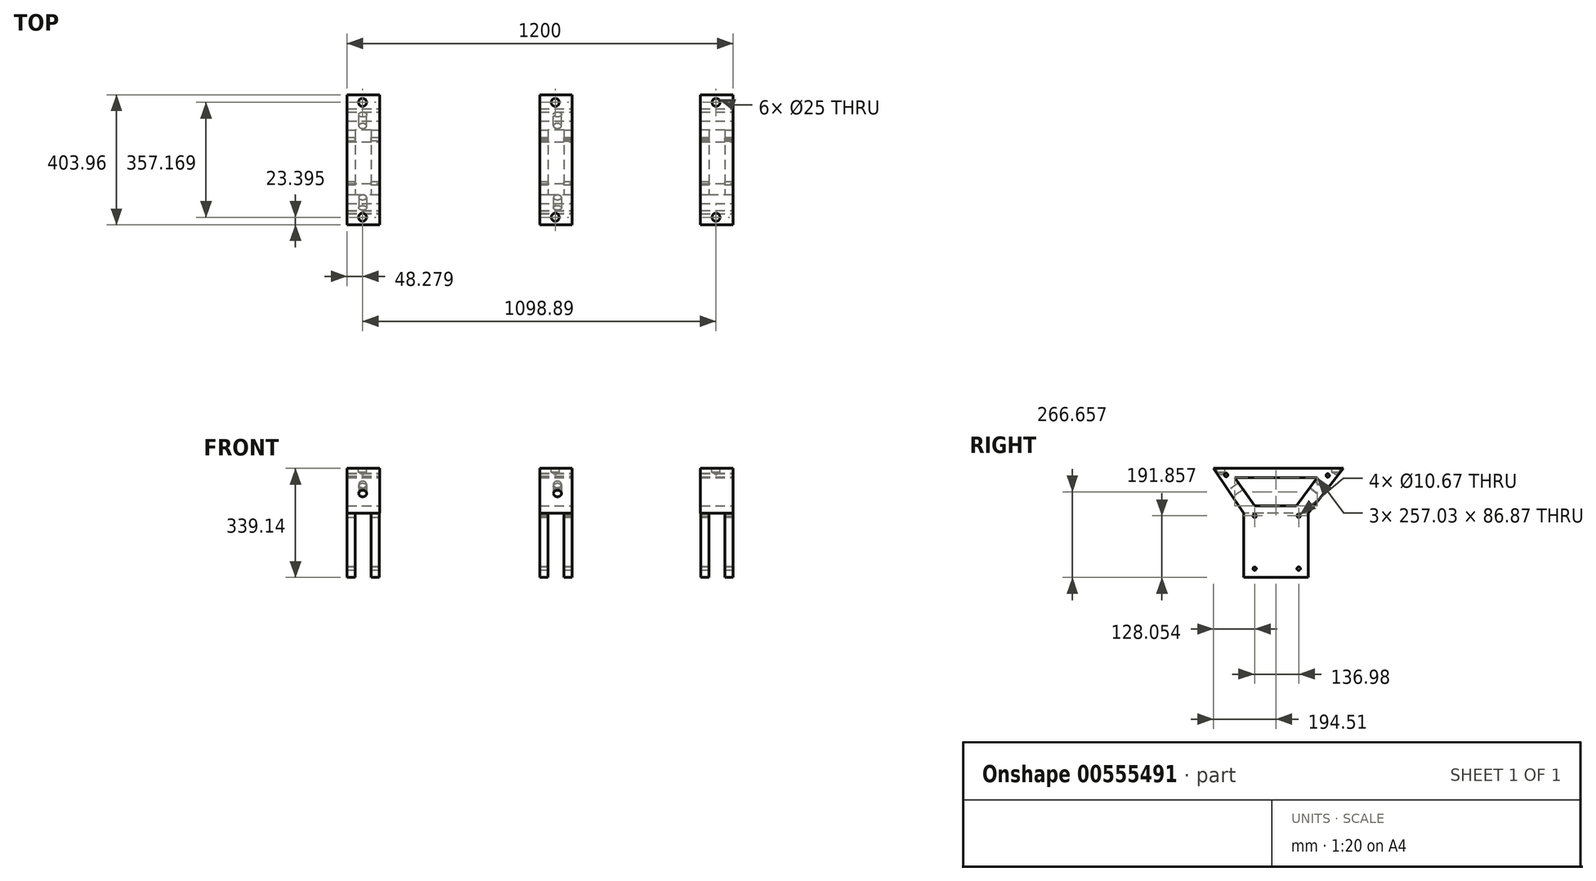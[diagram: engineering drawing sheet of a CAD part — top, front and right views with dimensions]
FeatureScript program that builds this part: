
annotation { "Feature Type Name" : "Feature", "Feature Type Description" : "" }
export const myFeature = defineFeature(function(context is Context, id is Id, definition is map)
    precondition{}
    {
        {
            var Q0;
            Q0=qCreatedBy(makeId("Front.planeOp"),FACE);
            var sketch = newSketch(context, id + "F0", { "sketchPlane" : qUnion([Q0])});
            skLineSegment(sketch, "E0.bottom", {"start": v(-163.42, 57.04) * mm, "end": v(-63.42, 57.04) * mm});
            skLineSegment(sketch, "E0.top", {"start": v(-163.42, -142.96) * mm, "end": v(-63.42, -142.96) * mm});
            skLineSegment(sketch, "E0.left", {"start": v(-163.42, 57.04) * mm, "end": v(-163.42, -142.96) * mm});
            skLineSegment(sketch, "E0.right", {"start": v(-63.42, 57.04) * mm, "end": v(-63.42, -142.96) * mm});
            skLineSegment(sketch, "E1.bottom", {"start": v(936.58, 57.04) * mm, "end": v(1036.58, 57.04) * mm});
            skLineSegment(sketch, "E1.top", {"start": v(936.58, -142.96) * mm, "end": v(1036.58, -142.96) * mm});
            skLineSegment(sketch, "E1.left", {"start": v(936.58, 57.04) * mm, "end": v(936.58, -142.96) * mm});
            skLineSegment(sketch, "E1.right", {"start": v(1036.58, 57.04) * mm, "end": v(1036.58, -142.96) * mm});
            skLineSegment(sketch, "E2.bottom", {"start": v(436.58, 57.04) * mm, "end": v(536.58, 57.04) * mm});
            skLineSegment(sketch, "E2.top", {"start": v(436.58, -142.96) * mm, "end": v(536.58, -142.96) * mm});
            skLineSegment(sketch, "E2.left", {"start": v(436.58, 57.04) * mm, "end": v(436.58, -142.96) * mm});
            skLineSegment(sketch, "E2.right", {"start": v(536.58, 57.04) * mm, "end": v(536.58, -142.96) * mm});
            skSolve(sketch);
        }
        {
            var Q0;
            Q0 = qSketchRegion(id + "F0", true);
            extrude(context, id + "F1", {"entities" : qUnion([Q0]), "depth" : 200 * mm, "offsetDistance" : 25 * mm});
        }
        {
            var Q0;
            Q0=makeQuery(id+"F1.opExtrude","SWEPT_FACE",FACE,{"disambiguationData":[OSD([sQuery(id+"F0.wireOp",EDGE,"E1.right")])]});
            var sketch = newSketch(context, id + "F2", { "sketchPlane" : qUnion([Q0])});
            skSolve(sketch);
        }
        {
            var Q0;
            {var subQ0=sQuery(id+"F0.wireOp",EDGE,"E1.right");Q0=makeQuery(id+"F2.imprint","IMPRINT",FACE,{"disambiguationData":[TD([[makeQuery(id+"F2.imprint","IMPRINT",EDGE,{"derivedFrom":makeQuery(id+"F1.opExtrude","CAP_EDGE",EDGE,{"disambiguationData":[OSD([subQ0])],"isStart":true})}),-1.0]])]});}
            var sketch = newSketch(context, id + "F3", { "sketchPlane" : qUnion([Q0])});
            skLineSegment(sketch, "E3", {"start": v(-199.96, 56.98) * mm, "end": v(-294.17, 196.18) * mm});
            skLineSegment(sketch, "E4", {"start": v(0, 56.94) * mm, "end": v(109.79, 196.18) * mm});
            skLineSegment(sketch, "E5", {"start": v(109.79, 196.18) * mm, "end": v(-294.17, 196.18) * mm});
            skLineSegment(sketch, "E6", {"start": v(-199.96, 56.98) * mm, "end": v(-96.96, 56.9) * mm});
            skLineSegment(sketch, "E7", {"start": v(-96.96, 56.9) * mm, "end": v(0, 56.94) * mm});
            skSolve(sketch);
        }
        {
            var Q0;
            Q0 = qSketchRegion(id + "F3", true);
            extrude(context, id + "F4", {"entities" : qUnion([Q0]), "oppositeDirection" : true, "depth" : 1200 * mm, "offsetDistance" : 25 * mm});
        }
        {
            var Q0;
            Q0=makeQuery(id+"F4.opExtrude","CAP_FACE",FACE,{"disambiguationData":[OSD([sQuery(id+"F3.wireOp",EDGE,"E3"),sQuery(id+"F3.wireOp",EDGE,"E4"),sQuery(id+"F3.wireOp",EDGE,"E5"),sQuery(id+"F3.wireOp",EDGE,"E6"),sQuery(id+"F3.wireOp",EDGE,"E7")])],"isStart":true});
            var sketch = newSketch(context, id + "F5", { "sketchPlane" : qUnion([Q0])});
            skLineSegment(sketch, "E8", {"start": v(-228.17, 167.13) * mm, "end": v(28.85, 167.13) * mm});
            skLineSegment(sketch, "E9", {"start": v(28.85, 167.13) * mm, "end": v(-36.76, 80.26) * mm});
            skLineSegment(sketch, "E10", {"start": v(-36.76, 80.26) * mm, "end": v(-166.23, 80.26) * mm});
            skLineSegment(sketch, "E11", {"start": v(-166.23, 80.26) * mm, "end": v(-228.17, 167.13) * mm});
            skSolve(sketch);
        }
        {
            var Q0;
            Q0 = qSketchRegion(id + "F5", true);
            extrude(context, id + "F6", {"entities" : qUnion([Q0]), "operationType" : NewBodyOperationType.REMOVE, "endBound" : BoundingType.THROUGH_ALL, "oppositeDirection" : true, "depth" : 25 * mm, "offsetDistance" : 25 * mm});
        }
        {
            var Q0;
            Q0=makeQuery(id+"F4.opExtrude","SWEPT_FACE",FACE,{"disambiguationData":[OSD([sQuery(id+"F3.wireOp",EDGE,"E3")])]});
            var sketch = newSketch(context, id + "F7", { "sketchPlane" : qUnion([Q0])});
            skLineSegment(sketch, "E12", {"start": v(-62.3, -22.73) * mm, "end": v(-62.3, 343.78) * mm});
            skLineSegment(sketch, "E13", {"start": v(435.52, -29.2) * mm, "end": v(435.52, 412.26) * mm});
            skLineSegment(sketch, "E14", {"start": v(435.52, 412.26) * mm, "end": v(-62.3, 343.78) * mm});
            skLineSegment(sketch, "E15", {"start": v(-62.3, -22.73) * mm, "end": v(435.52, -29.2) * mm});
            skSolve(sketch);
        }
        {
            var Q0;
            Q0 = qSketchRegion(id + "F7", true);
            extrude(context, id + "F8", {"entities" : qUnion([Q0]), "operationType" : NewBodyOperationType.REMOVE, "endBound" : BoundingType.THROUGH_ALL, "oppositeDirection" : true, "depth" : 25 * mm, "offsetDistance" : 25 * mm});
        }
        {
            var Q0;
            {var subQ2=sQuery(id+"F3.wireOp",EDGE,"E3");Q0=makeQuery(id+"F8.boolean.opBoolean","SPLIT",FACE,{"disambiguationData":[TD([makeQuery(id+"F8.opExtrude","SWEPT_FACE",FACE,{"disambiguationData":[OSD([sQuery(id+"F7.wireOp",EDGE,"E13")])]})])],"derivedFrom":makeQuery(id+"F4.opExtrude","SWEPT_FACE",FACE,{"disambiguationData":[OSD([subQ2])]})});}
            var sketch = newSketch(context, id + "F9", { "sketchPlane" : qUnion([Q0])});
            skLineSegment(sketch, "E16", {"start": v(536.96, 159.26) * mm, "end": v(536.96, 342.97) * mm});
            skLineSegment(sketch, "E17", {"start": v(935.8, 159.26) * mm, "end": v(935.8, 344.13) * mm});
            skLineSegment(sketch, "E18", {"start": v(935.8, 344.13) * mm, "end": v(536.96, 342.97) * mm});
            skLineSegment(sketch, "E19", {"start": v(536.96, 159.26) * mm, "end": v(536.96, -439.08) * mm});
            skLineSegment(sketch, "E20", {"start": v(536.96, -439.08) * mm, "end": v(935.8, -439.08) * mm});
            skLineSegment(sketch, "E21", {"start": v(935.8, -439.08) * mm, "end": v(935.8, 159.26) * mm});
            skSolve(sketch);
        }
        {
            var Q0;
            Q0 = qSketchRegion(id + "F9", true);
            extrude(context, id + "F10", {"entities" : qUnion([Q0]), "operationType" : NewBodyOperationType.REMOVE, "oppositeDirection" : true, "depth" : 425 * mm, "offsetDistance" : 25 * mm});
        }
        {
            var Q0;
            {var subQ1=sQuery(id+"F3.wireOp",EDGE,"E5");Q0=makeQuery(id+"F8.boolean.opBoolean","SPLIT",FACE,{"disambiguationData":[TD([makeQuery(id+"F8.opExtrude","SWEPT_FACE",FACE,{"disambiguationData":[OSD([sQuery(id+"F7.wireOp",EDGE,"E12")])]})])],"derivedFrom":makeQuery(id+"F4.opExtrude","SWEPT_FACE",FACE,{"disambiguationData":[OSD([subQ1])]})});}
            var sketch = newSketch(context, id + "F11", { "sketchPlane" : qUnion([Q0])});
            skCircle(sketch, "E22", {"center": v(-115.14, 86.4) * mm, "radius": 12.4 * mm});
            skCircle(sketch, "E23", {"center": v(-115.14, -270.77) * mm, "radius": 12.4 * mm});
            skCircle(sketch, "E24.1.0.0", {"center": v(484.12, 86.4) * mm, "radius": 12.4 * mm});
            skCircle(sketch, "E24.1.0.1", {"center": v(484.12, -270.77) * mm, "radius": 12.4 * mm});
            skCircle(sketch, "E24.2.0.0", {"center": v(983.75, 86.4) * mm, "radius": 12.4 * mm});
            skCircle(sketch, "E24.2.0.1", {"center": v(983.75, -270.77) * mm, "radius": 12.4 * mm});
            skSolve(sketch);
        }
        {
            var Q0;
            Q0=sQuery(id+"F11.wireOp",VERTEX,"E22.center");
            var Q1;
            Q1=sQuery(id+"F11.wireOp",VERTEX,"E23.center");
            var Q2;
            Q2=sQuery(id+"F11.wireOp",VERTEX,"E24.1.0.1.center");
            var Q3;
            Q3=sQuery(id+"F11.wireOp",VERTEX,"E24.1.0.0.center");
            var Q4;
            Q4=sQuery(id+"F11.wireOp",VERTEX,"E24.2.0.0.center");
            var Q5;
            Q5=sQuery(id+"F11.wireOp",VERTEX,"E24.2.0.1.center");
            var Q6;
            Q6=makeQuery(id+"F8.boolean.opBoolean","SPLIT",BODY,{"disambiguationData":[OD(1.0)],"derivedFrom":makeQuery(id+"F4.opExtrude","SWEPT_BODY",BODY,{"disambiguationData":[OSD([sQuery(id+"F3.wireOp",EDGE,"E3"),sQuery(id+"F3.wireOp",EDGE,"E4"),sQuery(id+"F3.wireOp",EDGE,"E5"),sQuery(id+"F3.wireOp",EDGE,"E6"),sQuery(id+"F3.wireOp",EDGE,"E7")])]})});
            var Q7;
            Q7=makeQuery(id+"F10.boolean.opBoolean","SPLIT",BODY,{"disambiguationData":[OD(1.0)],"derivedFrom":makeQuery(id+"F8.boolean.opBoolean","SPLIT",BODY,{"disambiguationData":[OD(0.0)],"derivedFrom":makeQuery(id+"F4.opExtrude","SWEPT_BODY",BODY,{"disambiguationData":[OSD([sQuery(id+"F3.wireOp",EDGE,"E3"),sQuery(id+"F3.wireOp",EDGE,"E4"),sQuery(id+"F3.wireOp",EDGE,"E5"),sQuery(id+"F3.wireOp",EDGE,"E6"),sQuery(id+"F3.wireOp",EDGE,"E7")])]})})});
            var Q8;
            Q8=makeQuery(id+"F10.boolean.opBoolean","SPLIT",BODY,{"disambiguationData":[OD(0.0)],"derivedFrom":makeQuery(id+"F8.boolean.opBoolean","SPLIT",BODY,{"disambiguationData":[OD(0.0)],"derivedFrom":makeQuery(id+"F4.opExtrude","SWEPT_BODY",BODY,{"disambiguationData":[OSD([sQuery(id+"F3.wireOp",EDGE,"E3"),sQuery(id+"F3.wireOp",EDGE,"E4"),sQuery(id+"F3.wireOp",EDGE,"E5"),sQuery(id+"F3.wireOp",EDGE,"E6"),sQuery(id+"F3.wireOp",EDGE,"E7")])]})})});
            hole(context, id + "F12", {"style" : HoleStyle.SIMPLE, "endStyle" : HoleEndStyle.BLIND, "holeDiameter" : 25 * mm, "holeDepth" : 12 * mm, "isTappedThrough" : true, "tappedDepth" : 12 * mm, "tapClearance" : 3, "locations" : qUnion([Q0, Q1, Q2, Q3, Q4, Q5]), "scope" : qUnion([Q6, Q7, Q8])});
        }
        {
            var Q0;
            Q0=makeQuery(id+"F10.boolean.opBoolean","SPLIT",BODY,{"disambiguationData":[OD(1.0)],"derivedFrom":makeQuery(id+"F8.boolean.opBoolean","SPLIT",BODY,{"disambiguationData":[OD(0.0)],"derivedFrom":makeQuery(id+"F4.opExtrude","SWEPT_BODY",BODY,{"disambiguationData":[OSD([sQuery(id+"F3.wireOp",EDGE,"E3"),sQuery(id+"F3.wireOp",EDGE,"E4"),sQuery(id+"F3.wireOp",EDGE,"E5"),sQuery(id+"F3.wireOp",EDGE,"E6"),sQuery(id+"F3.wireOp",EDGE,"E7")])]})})});
            var Q1;
            Q1=makeQuery(id+"F1.opExtrude","SWEPT_BODY",BODY,{"disambiguationData":[OSD([sQuery(id+"F0.wireOp",EDGE,"E2.bottom"),sQuery(id+"F0.wireOp",EDGE,"E2.top"),sQuery(id+"F0.wireOp",EDGE,"E2.left"),sQuery(id+"F0.wireOp",EDGE,"E2.right")])]});
            var Q2;
            Q2=makeQuery(id+"F10.boolean.opBoolean","SPLIT",BODY,{"disambiguationData":[OD(0.0)],"derivedFrom":makeQuery(id+"F8.boolean.opBoolean","SPLIT",BODY,{"disambiguationData":[OD(0.0)],"derivedFrom":makeQuery(id+"F4.opExtrude","SWEPT_BODY",BODY,{"disambiguationData":[OSD([sQuery(id+"F3.wireOp",EDGE,"E3"),sQuery(id+"F3.wireOp",EDGE,"E4"),sQuery(id+"F3.wireOp",EDGE,"E5"),sQuery(id+"F3.wireOp",EDGE,"E6"),sQuery(id+"F3.wireOp",EDGE,"E7")])]})})});
            var Q3;
            Q3=makeQuery(id+"F1.opExtrude","SWEPT_BODY",BODY,{"disambiguationData":[OSD([sQuery(id+"F0.wireOp",EDGE,"E1.bottom"),sQuery(id+"F0.wireOp",EDGE,"E1.top"),sQuery(id+"F0.wireOp",EDGE,"E1.left"),sQuery(id+"F0.wireOp",EDGE,"E1.right")])]});
            var Q4;
            Q4=makeQuery(id+"F8.boolean.opBoolean","SPLIT",BODY,{"disambiguationData":[OD(1.0)],"derivedFrom":makeQuery(id+"F4.opExtrude","SWEPT_BODY",BODY,{"disambiguationData":[OSD([sQuery(id+"F3.wireOp",EDGE,"E3"),sQuery(id+"F3.wireOp",EDGE,"E4"),sQuery(id+"F3.wireOp",EDGE,"E5"),sQuery(id+"F3.wireOp",EDGE,"E6"),sQuery(id+"F3.wireOp",EDGE,"E7")])]})});
            var Q5;
            Q5=makeQuery(id+"F1.opExtrude","SWEPT_BODY",BODY,{"disambiguationData":[OSD([sQuery(id+"F0.wireOp",EDGE,"E0.bottom"),sQuery(id+"F0.wireOp",EDGE,"E0.top"),sQuery(id+"F0.wireOp",EDGE,"E0.left"),sQuery(id+"F0.wireOp",EDGE,"E0.right")])]});
            booleanBodies(context, id + "F13", {"operationType" : BooleanOperationType.UNION, "tools" : qUnion([Q0, Q1, Q2, Q3, Q4, Q5])});
        }
        {
            var Q0;
            Q0=makeQuery(id+"F13.opBoolean","MERGE",FACE,{"derivedFrom":[makeQuery(id+"F1.opExtrude","SWEPT_FACE",FACE,{"disambiguationData":[OSD([sQuery(id+"F0.wireOp",EDGE,"E0.left")])]}),makeQuery(id+"F4.opExtrude","CAP_FACE",FACE,{"disambiguationData":[OSD([sQuery(id+"F3.wireOp",EDGE,"E3"),sQuery(id+"F3.wireOp",EDGE,"E4"),sQuery(id+"F3.wireOp",EDGE,"E5"),sQuery(id+"F3.wireOp",EDGE,"E6"),sQuery(id+"F3.wireOp",EDGE,"E7")])],"isStart":false})]});
            var sketch = newSketch(context, id + "F14", { "sketchPlane" : qUnion([Q0])});
            skCircle(sketch, "E25", {"center": v(29.14, 48.9) * mm, "radius": 5.34 * mm});
            skCircle(sketch, "E26", {"center": v(166.12, 48.9) * mm, "radius": 5.34 * mm});
            skCircle(sketch, "E27", {"center": v(29.14, -115.26) * mm, "radius": 5.35 * mm});
            skCircle(sketch, "E28", {"center": v(166.12, -115.26) * mm, "radius": 5.05 * mm});
            skSolve(sketch);
        }
        {
            var Q0;
            Q0=makeQuery(id+"F14.imprint","IMPRINT",FACE,{"disambiguationData":[TD([[makeQuery(id+"F14.imprint","IMPRINT",EDGE,{"derivedFrom":sQuery(id+"F14.wireOp",EDGE,"E26")}),1.0]])]});
            var Q1;
            Q1=makeQuery(id+"F14.imprint","IMPRINT",FACE,{"disambiguationData":[TD([[makeQuery(id+"F14.imprint","IMPRINT",EDGE,{"derivedFrom":sQuery(id+"F14.wireOp",EDGE,"E27")}),1.0]])]});
            var Q2;
            Q2=makeQuery(id+"F14.imprint","IMPRINT",FACE,{"disambiguationData":[TD([[makeQuery(id+"F14.imprint","IMPRINT",EDGE,{"derivedFrom":sQuery(id+"F14.wireOp",EDGE,"E28")}),1.0]])]});
            var Q3;
            Q3=makeQuery(id+"F14.imprint","IMPRINT",FACE,{"disambiguationData":[TD([[makeQuery(id+"F14.imprint","IMPRINT",EDGE,{"derivedFrom":sQuery(id+"F14.wireOp",EDGE,"E25")}),1.0]])]});
            extrude(context, id + "F15", {"entities" : qUnion([Q0, Q1, Q2, Q3]), "operationType" : NewBodyOperationType.REMOVE, "endBound" : BoundingType.THROUGH_ALL, "oppositeDirection" : true, "depth" : 25 * mm, "offsetDistance" : 25 * mm});
        }
        {
            var Q0;
            Q0=makeQuery(id+"F1.opExtrude","SWEPT_FACE",FACE,{"disambiguationData":[OSD([sQuery(id+"F0.wireOp",EDGE,"E2.left")])]});
            var sketch = newSketch(context, id + "F16", { "sketchPlane" : qUnion([Q0])});
            skCircle(sketch, "E29", {"center": v(29.07, 48.87) * mm, "radius": 5.34 * mm});
            skCircle(sketch, "E30", {"center": v(166.1, 48.83) * mm, "radius": 5.34 * mm});
            skCircle(sketch, "E31", {"center": v(166.1, -115.28) * mm, "radius": 5.05 * mm});
            skCircle(sketch, "E32", {"center": v(29.2, -115.26) * mm, "radius": 5.34 * mm});
            skSolve(sketch);
        }
        {
            var Q0;
            Q0 = qSketchRegion(id + "F16", true);
            extrude(context, id + "F17", {"entities" : qUnion([Q0]), "operationType" : NewBodyOperationType.REMOVE, "endBound" : BoundingType.THROUGH_ALL, "oppositeDirection" : true, "depth" : 25 * mm, "offsetDistance" : 25 * mm});
        }
        {
            var Q0;
            Q0=makeQuery(id+"F1.opExtrude","SWEPT_FACE",FACE,{"disambiguationData":[OSD([sQuery(id+"F0.wireOp",EDGE,"E1.left")])]});
            var sketch = newSketch(context, id + "F18", { "sketchPlane" : qUnion([Q0])});
            skCircle(sketch, "E33", {"center": v(166.08, 48.88) * mm, "radius": 5.34 * mm});
            skCircle(sketch, "E34", {"center": v(29.16, 48.9) * mm, "radius": 5.34 * mm});
            skCircle(sketch, "E35", {"center": v(29.12, -115.26) * mm, "radius": 5.34 * mm});
            skCircle(sketch, "E36", {"center": v(166.08, -115.29) * mm, "radius": 5.02 * mm});
            skSolve(sketch);
        }
        {
            var Q0;
            Q0 = qSketchRegion(id + "F18", true);
            extrude(context, id + "F19", {"entities" : qUnion([Q0]), "operationType" : NewBodyOperationType.REMOVE, "endBound" : BoundingType.THROUGH_ALL, "oppositeDirection" : true, "depth" : 1250 * mm, "offsetDistance" : 25 * mm});
        }
        {
            var Q0;
            {var subQ2=sQuery(id+"F3.wireOp",EDGE,"E3");Q0=makeQuery(id+"F8.boolean.opBoolean","SPLIT",FACE,{"disambiguationData":[TD([makeQuery(id+"F8.opExtrude","SWEPT_FACE",FACE,{"disambiguationData":[OSD([sQuery(id+"F7.wireOp",EDGE,"E12")])]})])],"derivedFrom":makeQuery(id+"F4.opExtrude","SWEPT_FACE",FACE,{"disambiguationData":[OSD([subQ2])]})});}
            var sketch = newSketch(context, id + "F20", { "sketchPlane" : qUnion([Q0])});
            skCircle(sketch, "E37", {"center": v(-114.59, 233.48) * mm, "radius": 10.87 * mm});
            skCircle(sketch, "E38", {"center": v(490.96, 233.48) * mm, "radius": 10.87 * mm});
            skSolve(sketch);
        }
        {
            var Q0;
            Q0=sQuery(id+"F20.wireOp",VERTEX,"E37.center");
            var Q1;
            Q1=sQuery(id+"F20.wireOp",VERTEX,"E38.center");
            var Q2;
            Q2=makeQuery(id+"F8.boolean.opBoolean","SPLIT",BODY,{"disambiguationData":[OD(1.0)],"derivedFrom":makeQuery(id+"F4.opExtrude","SWEPT_BODY",BODY,{"disambiguationData":[OSD([sQuery(id+"F3.wireOp",EDGE,"E3"),sQuery(id+"F3.wireOp",EDGE,"E4"),sQuery(id+"F3.wireOp",EDGE,"E5"),sQuery(id+"F3.wireOp",EDGE,"E6"),sQuery(id+"F3.wireOp",EDGE,"E7")])]})});
            var Q3;
            Q3=makeQuery(id+"F10.boolean.opBoolean","SPLIT",BODY,{"disambiguationData":[OD(1.0)],"derivedFrom":makeQuery(id+"F8.boolean.opBoolean","SPLIT",BODY,{"disambiguationData":[OD(0.0)],"derivedFrom":makeQuery(id+"F4.opExtrude","SWEPT_BODY",BODY,{"disambiguationData":[OSD([sQuery(id+"F3.wireOp",EDGE,"E3"),sQuery(id+"F3.wireOp",EDGE,"E4"),sQuery(id+"F3.wireOp",EDGE,"E5"),sQuery(id+"F3.wireOp",EDGE,"E6"),sQuery(id+"F3.wireOp",EDGE,"E7")])]})})});
            hole(context, id + "F21", {"style" : HoleStyle.SIMPLE, "endStyle" : HoleEndStyle.BLIND, "holeDiameter" : 25 * mm, "majorDiameter" : 5 * mm, "holeDepth" : 50 * mm, "isTappedThrough" : true, "tappedDepth" : 12 * mm, "tapClearance" : 3, "locations" : qUnion([Q0, Q1]), "scope" : qUnion([Q2, Q3])});
        }
        {
            var Q0;
            {var subQ2=sQuery(id+"F3.wireOp",EDGE,"E4");Q0=makeQuery(id+"F8.boolean.opBoolean","SPLIT",FACE,{"disambiguationData":[TD([makeQuery(id+"F8.opExtrude","SWEPT_FACE",FACE,{"disambiguationData":[OSD([sQuery(id+"F7.wireOp",EDGE,"E12")])]})])],"derivedFrom":makeQuery(id+"F4.opExtrude","SWEPT_FACE",FACE,{"disambiguationData":[OSD([subQ2])]})});}
            var sketch = newSketch(context, id + "F22", { "sketchPlane" : qUnion([Q0])});
            skCircle(sketch, "E39", {"center": v(114.65, 122.94) * mm, "radius": 11.4 * mm});
            skCircle(sketch, "E40", {"center": v(-490.77, 123.31) * mm, "radius": 10.98 * mm});
            skSolve(sketch);
        }
        {
            var Q0;
            Q0=sQuery(id+"F22.wireOp",VERTEX,"E40.center");
            var Q1;
            Q1=sQuery(id+"F22.wireOp",VERTEX,"E39.center");
            var Q2;
            Q2=makeQuery(id+"F8.boolean.opBoolean","SPLIT",BODY,{"disambiguationData":[OD(1.0)],"derivedFrom":makeQuery(id+"F4.opExtrude","SWEPT_BODY",BODY,{"disambiguationData":[OSD([sQuery(id+"F3.wireOp",EDGE,"E3"),sQuery(id+"F3.wireOp",EDGE,"E4"),sQuery(id+"F3.wireOp",EDGE,"E5"),sQuery(id+"F3.wireOp",EDGE,"E6"),sQuery(id+"F3.wireOp",EDGE,"E7")])]})});
            var Q3;
            Q3=makeQuery(id+"F10.boolean.opBoolean","SPLIT",BODY,{"disambiguationData":[OD(1.0)],"derivedFrom":makeQuery(id+"F8.boolean.opBoolean","SPLIT",BODY,{"disambiguationData":[OD(0.0)],"derivedFrom":makeQuery(id+"F4.opExtrude","SWEPT_BODY",BODY,{"disambiguationData":[OSD([sQuery(id+"F3.wireOp",EDGE,"E3"),sQuery(id+"F3.wireOp",EDGE,"E4"),sQuery(id+"F3.wireOp",EDGE,"E5"),sQuery(id+"F3.wireOp",EDGE,"E6"),sQuery(id+"F3.wireOp",EDGE,"E7")])]})})});
            hole(context, id + "F23", {"style" : HoleStyle.SIMPLE, "endStyle" : HoleEndStyle.BLIND, "holeDiameter" : 25 * mm, "majorDiameter" : 5 * mm, "holeDepth" : 50 * mm, "isTappedThrough" : true, "tappedDepth" : 12 * mm, "tapClearance" : 3, "locations" : qUnion([Q0, Q1]), "scope" : qUnion([Q2, Q3])});
        }
        {
            var Q0;
            Q0=makeQuery(id+"F13.opBoolean","MERGE",FACE,{"derivedFrom":[makeQuery(id+"F1.opExtrude","SWEPT_FACE",FACE,{"disambiguationData":[OSD([sQuery(id+"F0.wireOp",EDGE,"E1.right")])]}),makeQuery(id+"F4.opExtrude","CAP_FACE",FACE,{"disambiguationData":[OSD([sQuery(id+"F3.wireOp",EDGE,"E3"),sQuery(id+"F3.wireOp",EDGE,"E4"),sQuery(id+"F3.wireOp",EDGE,"E5"),sQuery(id+"F3.wireOp",EDGE,"E6"),sQuery(id+"F3.wireOp",EDGE,"E7")])],"isStart":true})]});
            var sketch = newSketch(context, id + "F24", { "sketchPlane" : qUnion([Q0])});
            skCircle(sketch, "E41", {"center": v(61.14, 174.4) * mm, "radius": 5.28 * mm});
            skSolve(sketch);
        }
        {
            var Q0;
            Q0 = qSketchRegion(id + "F24", true);
            extrude(context, id + "F25", {"entities" : qUnion([Q0]), "operationType" : NewBodyOperationType.REMOVE, "endBound" : BoundingType.THROUGH_ALL, "oppositeDirection" : true, "depth" : 25 * mm, "offsetDistance" : 25 * mm});
        }
        {
            var Q0;
            Q0=makeQuery(id+"F10.boolean.opBoolean","COPY",FACE,{"derivedFrom":makeQuery(id+"F10.opExtrude","SWEPT_FACE",FACE,{"disambiguationData":[OSD([sQuery(id+"F9.wireOp",EDGE,"E16"),sQuery(id+"F9.wireOp",EDGE,"E19")])]})});
            var sketch = newSketch(context, id + "F26", { "sketchPlane" : qUnion([Q0])});
            skCircle(sketch, "E42", {"center": v(61.14, 174.44) * mm, "radius": 5.15 * mm});
            skSolve(sketch);
        }
        {
            var Q0;
            Q0 = qSketchRegion(id + "F26", true);
            extrude(context, id + "F27", {"entities" : qUnion([Q0]), "operationType" : NewBodyOperationType.REMOVE, "endBound" : BoundingType.THROUGH_ALL, "oppositeDirection" : true, "depth" : 25 * mm, "offsetDistance" : 25 * mm});
        }
        {
            var Q0;
            Q0=makeQuery(id+"F8.boolean.opBoolean","COPY",FACE,{"derivedFrom":makeQuery(id+"F8.opExtrude","SWEPT_FACE",FACE,{"disambiguationData":[OSD([sQuery(id+"F7.wireOp",EDGE,"E12")])]})});
            var sketch = newSketch(context, id + "F28", { "sketchPlane" : qUnion([Q0])});
            skCircle(sketch, "E43", {"center": v(61.18, 174.42) * mm, "radius": 5.25 * mm});
            skSolve(sketch);
        }
        {
            var Q0;
            Q0 = qSketchRegion(id + "F28", true);
            extrude(context, id + "F29", {"entities" : qUnion([Q0]), "operationType" : NewBodyOperationType.REMOVE, "endBound" : BoundingType.THROUGH_ALL, "oppositeDirection" : true, "depth" : 25 * mm, "offsetDistance" : 25 * mm});
        }
        {
            var Q0;
            Q0=makeQuery(id+"F13.opBoolean","MERGE",FACE,{"derivedFrom":[makeQuery(id+"F1.opExtrude","SWEPT_FACE",FACE,{"disambiguationData":[OSD([sQuery(id+"F0.wireOp",EDGE,"E1.right")])]}),makeQuery(id+"F4.opExtrude","CAP_FACE",FACE,{"disambiguationData":[OSD([sQuery(id+"F3.wireOp",EDGE,"E3"),sQuery(id+"F3.wireOp",EDGE,"E4"),sQuery(id+"F3.wireOp",EDGE,"E5"),sQuery(id+"F3.wireOp",EDGE,"E6"),sQuery(id+"F3.wireOp",EDGE,"E7")])],"isStart":true})]});
            var sketch = newSketch(context, id + "F30", { "sketchPlane" : qUnion([Q0])});
            skCircle(sketch, "E44", {"center": v(-254.8, 175.98) * mm, "radius": 5.61 * mm});
            skSolve(sketch);
        }
        {
            var Q0;
            Q0 = qSketchRegion(id + "F30", true);
            extrude(context, id + "F31", {"entities" : qUnion([Q0]), "operationType" : NewBodyOperationType.REMOVE, "endBound" : BoundingType.THROUGH_ALL, "oppositeDirection" : true, "depth" : 25 * mm, "offsetDistance" : 25 * mm});
        }
        {
            var Q0;
            Q0=makeQuery(id+"F10.boolean.opBoolean","COPY",FACE,{"derivedFrom":makeQuery(id+"F10.opExtrude","SWEPT_FACE",FACE,{"disambiguationData":[OSD([sQuery(id+"F9.wireOp",EDGE,"E16"),sQuery(id+"F9.wireOp",EDGE,"E19")])]})});
            var sketch = newSketch(context, id + "F32", { "sketchPlane" : qUnion([Q0])});
            skCircle(sketch, "E45", {"center": v(-254.85, 176.03) * mm, "radius": 5.61 * mm});
            skSolve(sketch);
        }
        {
            var Q0;
            Q0 = qSketchRegion(id + "F32", true);
            extrude(context, id + "F33", {"entities" : qUnion([Q0]), "operationType" : NewBodyOperationType.REMOVE, "endBound" : BoundingType.THROUGH_ALL, "oppositeDirection" : true, "depth" : 25 * mm, "offsetDistance" : 25 * mm});
        }
        {
            var Q0;
            Q0=makeQuery(id+"F8.boolean.opBoolean","COPY",FACE,{"derivedFrom":makeQuery(id+"F8.opExtrude","SWEPT_FACE",FACE,{"disambiguationData":[OSD([sQuery(id+"F7.wireOp",EDGE,"E12")])]})});
            var sketch = newSketch(context, id + "F34", { "sketchPlane" : qUnion([Q0])});
            skCircle(sketch, "E46", {"center": v(-254.82, 176) * mm, "radius": 5.56 * mm});
            skSolve(sketch);
        }
        {
            var Q0;
            Q0 = qSketchRegion(id + "F34", true);
            extrude(context, id + "F35", {"entities" : qUnion([Q0]), "operationType" : NewBodyOperationType.REMOVE, "endBound" : BoundingType.THROUGH_ALL, "oppositeDirection" : true, "depth" : 25 * mm, "offsetDistance" : 25 * mm});
        }
        {
            var Q0;
            Q0=makeQuery(id+"F1.opExtrude","CAP_FACE",FACE,{"disambiguationData":[OSD([sQuery(id+"F0.wireOp",EDGE,"E0.bottom"),sQuery(id+"F0.wireOp",EDGE,"E0.top"),sQuery(id+"F0.wireOp",EDGE,"E0.left"),sQuery(id+"F0.wireOp",EDGE,"E0.right")])],"isStart":false});
            var sketch = newSketch(context, id + "F36", { "sketchPlane" : qUnion([Q0])});
            skLineSegment(sketch, "E47", {"start": v(-163.42, 57.04) * mm, "end": v(-138.42, 57.04) * mm});
            skLineSegment(sketch, "E48", {"start": v(-63.42, 57.04) * mm, "end": v(-88.42, 57.04) * mm});
            skLineSegment(sketch, "E49", {"start": v(-138.42, 57.04) * mm, "end": v(-138.42, -142.96) * mm});
            skLineSegment(sketch, "E50", {"start": v(-138.42, -142.96) * mm, "end": v(-88.42, -142.96) * mm});
            skLineSegment(sketch, "E51", {"start": v(-88.42, -142.96) * mm, "end": v(-88.42, 57.04) * mm});
            skLineSegment(sketch, "E52", {"start": v(-138.42, 57.04) * mm, "end": v(-88.42, 57.04) * mm});
            skSolve(sketch);
        }
        {
            var Q0;
            Q0 = qSketchRegion(id + "F36", true);
            extrude(context, id + "F37", {"entities" : qUnion([Q0]), "operationType" : NewBodyOperationType.REMOVE, "oppositeDirection" : true, "depth" : 434 * mm, "offsetDistance" : 25 * mm});
        }
        {
            var Q0;
            Q0=makeQuery(id+"F1.opExtrude","CAP_FACE",FACE,{"disambiguationData":[OSD([sQuery(id+"F0.wireOp",EDGE,"E2.bottom"),sQuery(id+"F0.wireOp",EDGE,"E2.top"),sQuery(id+"F0.wireOp",EDGE,"E2.left"),sQuery(id+"F0.wireOp",EDGE,"E2.right")])],"isStart":false});
            var sketch = newSketch(context, id + "F38", { "sketchPlane" : qUnion([Q0])});
            skLineSegment(sketch, "E53", {"start": v(436.58, 57.04) * mm, "end": v(461.6, 57.04) * mm});
            skLineSegment(sketch, "E54", {"start": v(536.58, 57.04) * mm, "end": v(511.53, 57.04) * mm});
            skLineSegment(sketch, "E55", {"start": v(461.6, 57.04) * mm, "end": v(461.6, -142.96) * mm});
            skLineSegment(sketch, "E56", {"start": v(461.6, -142.96) * mm, "end": v(511.53, -142.96) * mm});
            skLineSegment(sketch, "E57", {"start": v(511.53, -142.96) * mm, "end": v(511.53, 57.04) * mm});
            skLineSegment(sketch, "E58", {"start": v(461.6, 57.04) * mm, "end": v(511.53, 57.04) * mm});
            skSolve(sketch);
        }
        {
            var Q0;
            Q0 = qSketchRegion(id + "F38", true);
            extrude(context, id + "F39", {"entities" : qUnion([Q0]), "operationType" : NewBodyOperationType.REMOVE, "oppositeDirection" : true, "depth" : 307 * mm, "offsetDistance" : 25 * mm});
        }
        {
            var Q0;
            Q0=makeQuery(id+"F1.opExtrude","CAP_FACE",FACE,{"disambiguationData":[OSD([sQuery(id+"F0.wireOp",EDGE,"E1.bottom"),sQuery(id+"F0.wireOp",EDGE,"E1.top"),sQuery(id+"F0.wireOp",EDGE,"E1.left"),sQuery(id+"F0.wireOp",EDGE,"E1.right")])],"isStart":false});
            var sketch = newSketch(context, id + "F40", { "sketchPlane" : qUnion([Q0])});
            skLineSegment(sketch, "E59", {"start": v(936.58, 57.04) * mm, "end": v(961.58, 57.04) * mm});
            skLineSegment(sketch, "E60", {"start": v(1036.58, 57.04) * mm, "end": v(1011.58, 57.04) * mm});
            skLineSegment(sketch, "E61", {"start": v(961.58, 57.04) * mm, "end": v(961.58, -142.96) * mm});
            skLineSegment(sketch, "E62", {"start": v(961.58, -142.96) * mm, "end": v(1011.58, -142.96) * mm});
            skLineSegment(sketch, "E63", {"start": v(1011.58, -142.96) * mm, "end": v(1011.58, 57.04) * mm});
            skLineSegment(sketch, "E64", {"start": v(961.58, 57.04) * mm, "end": v(1011.58, 57.04) * mm});
            skSolve(sketch);
        }
        {
            var Q0;
            Q0 = qSketchRegion(id + "F40", true);
            extrude(context, id + "F41", {"entities" : qUnion([Q0]), "operationType" : NewBodyOperationType.REMOVE, "oppositeDirection" : true, "depth" : 370 * mm, "offsetDistance" : 25 * mm});
        }
    });
